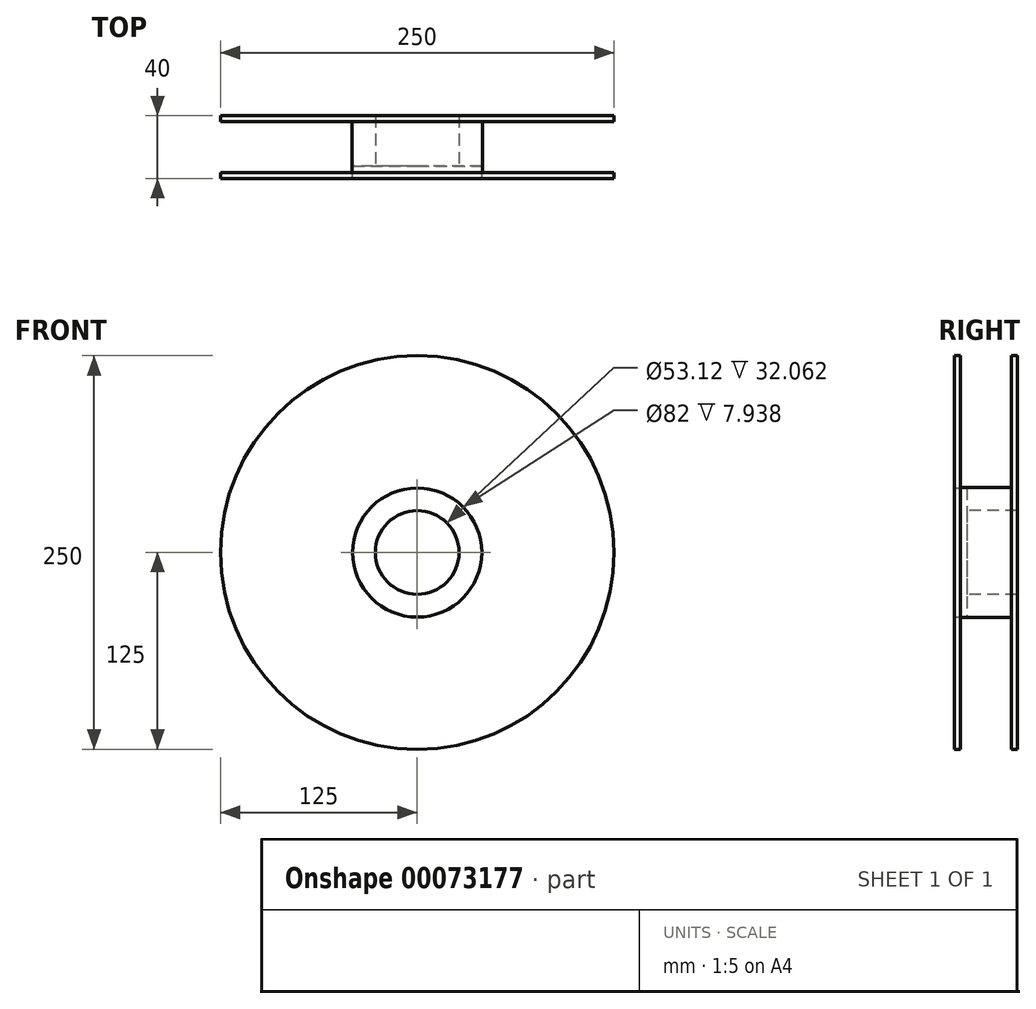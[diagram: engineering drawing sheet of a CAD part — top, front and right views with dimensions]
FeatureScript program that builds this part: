
annotation { "Feature Type Name" : "Feature", "Feature Type Description" : "" }
export const myFeature = defineFeature(function(context is Context, id is Id, definition is map)
    precondition{}
    {
        {
            var Q0;
            Q0=qCreatedBy(makeId("Front.planeOp"),FACE);
            var sketch = newSketch(context, id + "F0", { "sketchPlane" : qUnion([Q0])});
            skCircle(sketch, "E0", {"center": v(0, 0) * mm, "radius": 125 * mm});
            skSolve(sketch);
        }
        {
            var Q0;
            Q0=makeQuery(id+"F0.imprint","IMPRINT",FACE,{"disambiguationData":[TD([[makeQuery(id+"F0.imprint","IMPRINT",EDGE,{"derivedFrom":sQuery(id+"F0.wireOp",EDGE,"E0")}),1.0]])]});
            extrude(context, id + "F1", {"entities" : qUnion([Q0]), "endBound" : BoundingType.SYMMETRIC, "depth" : 40 * mm});
        }
        {
            var Q0;
            Q0=qCreatedBy(makeId("Front.planeOp"),FACE);
            var sketch = newSketch(context, id + "F2", { "sketchPlane" : qUnion([Q0])});
            skCircle(sketch, "E1", {"center": v(0, 0) * mm, "radius": 26.56 * mm});
            skSolve(sketch);
        }
        {
            var Q0;
            Q0 = qSketchRegion(id + "F2", true);
            extrude(context, id + "F3", {"entities" : qUnion([Q0]), "operationType" : NewBodyOperationType.REMOVE, "endBound" : BoundingType.SYMMETRIC, "oppositeDirection" : true, "depth" : 40 * mm});
        }
        {
            var Q0;
            Q0=qCreatedBy(makeId("Top.planeOp"),FACE);
            var sketch = newSketch(context, id + "F4", { "sketchPlane" : qUnion([Q0])});
            skLineSegment(sketch, "E2", {"start": v(0, 54.78) * mm, "end": v(0, -54.78) * mm, "construction": true});
            skSolve(sketch);
        }
        {
            var Q0;
            Q0=qCreatedBy(makeId("Top.planeOp"),FACE);
            var sketch = newSketch(context, id + "F5", { "sketchPlane" : qUnion([Q0])});
            skLineSegment(sketch, "E3.bottom", {"start": v(-128, 16.13) * mm, "end": v(-41.32, 16.13) * mm});
            skLineSegment(sketch, "E3.top", {"start": v(-128, -16.13) * mm, "end": v(-41.32, -16.13) * mm});
            skLineSegment(sketch, "E3.left", {"start": v(-128, 16.13) * mm, "end": v(-128, -16.13) * mm});
            skLineSegment(sketch, "E3.right", {"start": v(-41.32, 16.13) * mm, "end": v(-41.32, -16.13) * mm});
            skLineSegment(sketch, "E4", {"start": v(1.31, 0) * mm, "end": v(-150.57, 0) * mm, "construction": true});
            skSolve(sketch);
        }
        {
            var Q0;
            Q0 = qSketchRegion(id + "F5", true);
            var Q1;
            Q1=sQuery(id+"F4.wireOp",EDGE,"E2");
            revolve(context, id + "F6", {"operationType" : NewBodyOperationType.REMOVE, "entities" : qUnion([Q0]), "axis" : qUnion([Q1]), "revolveType" : RevolveType.FULL, "oppositeDirection" : true});
        }
        {
            var Q0;
            Q0=qCreatedBy(makeId("Right.planeOp"),FACE);
            var sketch = newSketch(context, id + "F7", { "sketchPlane" : qUnion([Q0])});
            skLineSegment(sketch, "E5", {"start": v(-20, 0) * mm, "end": v(-12.06, 0) * mm});
            skLineSegment(sketch, "E6", {"start": v(-12.06, 0) * mm, "end": v(-12.06, 41) * mm});
            skLineSegment(sketch, "E7", {"start": v(-12.06, 41) * mm, "end": v(-20, 41) * mm});
            skLineSegment(sketch, "E8", {"start": v(-20, 41) * mm, "end": v(-20, 0) * mm});
            skSolve(sketch);
        }
        {
            var Q0;
            Q0 = qSketchRegion(id + "F7", true);
            var Q1;
            Q1=sQuery(id+"F7.wireOp",EDGE,"E5");
            revolve(context, id + "F8", {"operationType" : NewBodyOperationType.REMOVE, "entities" : qUnion([Q0]), "axis" : qUnion([Q1]), "revolveType" : RevolveType.FULL, "oppositeDirection" : true});
        }
    });
